# Revit family: Legrand Cabinet Plexo³ 18 modules
name_source: partatom
category: Equipement électrique
revit_build: Autodesk Revit 2018 (Build: 20170223_1515(x64)
units: mm (PartAtom-declared; Revit-internal decimal feet)

## family parameters
Basée sur le plan de construction = Non
Configuration du panneau = Deux colonnes, circuits au sein
Cote de connecteur circulaire = Utiliser le diamètre
Couper avec des vides une fois chargée = Non
Numéro OmniClass = 23.80.30.11.17
Partagée = Non
Point de calcul de pièce = Non
Titre OmniClass = Distribution Boards and Control Panels
Toujours verticalement = Oui
Type d'élément = Tableau de raccordement

## types (18) — shared parameters
Cabinet 601835 = Non
ETIM Class 6.0 = EC000214
Fabricant = Legrand
General Conditions of Use = https://export.legrand.com
IK = 09
IP = 65
Image du type = plexo3_18_rangees_001926_pw_174335_pz_0.jpg
Material = Polystyrene
RAL = 7046
URL = www.legrand.fr

## per-type parameters (varying)
| type | Cabinet 001924 | Cabinet 001925 | Cabinet 001926 | Cabinet 001927 | Cabinet 601836 | Cabinet 601837 | Cabinet 601838 | Cabinet 601946 | Cabinet 601947 | Cabinet 601948 | Cabinet 601965 | Cabinet 601966 | Cabinet 601967 | Cabinet 601968 | Cabinet 601985 | Cabinet 601986 | Cabinet 601987 | Cabinet 601988 | Terminal block E | Terminal block N |
| Plexo³ 18 modules 1 row 001924 | Oui | Non | Non | Non | Non | Non | Non | Non | Non | Non | Non | Non | Non | Non | Non | Non | Non | Non | terminal block 5+18 holes |  |
| Plexo³ 18 modules 2 rows 001925 | Non | Oui | Non | Non | Non | Non | Non | Non | Non | Non | Non | Non | Non | Non | Non | Non | Non | Non | terminal block 5+27 holes |  |
| Plexo³ 18 modules 3 rows 001926 | Non | Non | Oui | Non | Non | Non | Non | Non | Non | Non | Non | Non | Non | Non | Non | Non | Non | Non | terminal block 5+36 holes |  |
| Plexo³ 18 modules 4 rows 001927 | Non | Non | Non | Oui | Non | Non | Non | Non | Non | Non | Non | Non | Non | Non | Non | Non | Non | Non | terminal block 5+45 holes |  |
| Plexo³ 18 modules 1 row 601965 | Non | Non | Non | Non | Non | Non | Non | Non | Non | Non | Oui | Non | Non | Non | Non | Non | Non | Non | terminal block 17 holes |  |
| Plexo³ 18 modules 1 row 601985 | Non | Non | Non | Non | Non | Non | Non | Non | Non | Non | Non | Non | Non | Non | Oui | Non | Non | Non | terminal block 17 holes | terminal block 17 holes |
| Plexo³ 18 modules 2 rows 601836 | Non | Non | Non | Non | Oui | Non | Non | Non | Non | Non | Non | Non | Non | Non | Non | Non | Non | Non |  |  |
| Plexo³ 18 modules 2 rows 601946 | Non | Non | Non | Non | Non | Non | Non | Oui | Non | Non | Non | Non | Non | Non | Non | Non | Non | Non |  |  |
| Plexo³ 18 modules 2 rows 601966 | Non | Non | Non | Non | Non | Non | Non | Non | Non | Non | Non | Oui | Non | Non | Non | Non | Non | Non | terminal block 22 holes |  |
| Plexo³ 18 modules 2 rows 601986 | Non | Non | Non | Non | Non | Non | Non | Non | Non | Non | Non | Non | Non | Non | Non | Oui | Non | Non | terminal block 22 holes | terminal block 22 holes |
| Plexo³ 18 modules 3 rows 601947 | Non | Non | Non | Non | Non | Non | Non | Non | Oui | Non | Non | Non | Non | Non | Non | Non | Non | Non |  |  |
| Plexo³ 18 modules 3 rows 601967 | Non | Non | Non | Non | Non | Non | Non | Non | Non | Non | Non | Non | Oui | Non | Non | Non | Non | Non | terminal blocks 27 holes |  |
| Plexo³ 18 modules 3 rows 601987 | Non | Non | Non | Non | Non | Non | Non | Non | Non | Non | Non | Non | Non | Non | Non | Non | Oui | Non | terminal blocks 27 holes | terminal blocks 27 holes |
| Plexo³ 18 modules 4 rows 601838 | Non | Non | Non | Non | Non | Non | Oui | Non | Non | Non | Non | Non | Non | Non | Non | Non | Non | Non |  |  |
| Plexo³ 18 modules 4 rows 601948 | Non | Non | Non | Non | Non | Non | Non | Non | Non | Oui | Non | Non | Non | Non | Non | Non | Non | Non |  |  |
| Plexo³ 18 modules 4 rows 601968 | Non | Non | Non | Non | Non | Non | Non | Non | Non | Non | Non | Non | Non | Oui | Non | Non | Non | Non | terminal block 35 holes |  |
| Plexo³ 18 modules 4 rows 601988 | Non | Non | Non | Non | Non | Non | Non | Non | Non | Non | Non | Non | Non | Non | Non | Non | Non | Oui | terminal block 35 holes | terminal block 35 holes |
| Plexo³ 18 modules 3 rows 601837 | Non | Non | Non | Non | Non | Oui | Non | Non | Non | Non | Non | Non | Non | Non | Non | Non | Non | Non |  |  |

note: column(s) folded — value = type name in every type: Description
